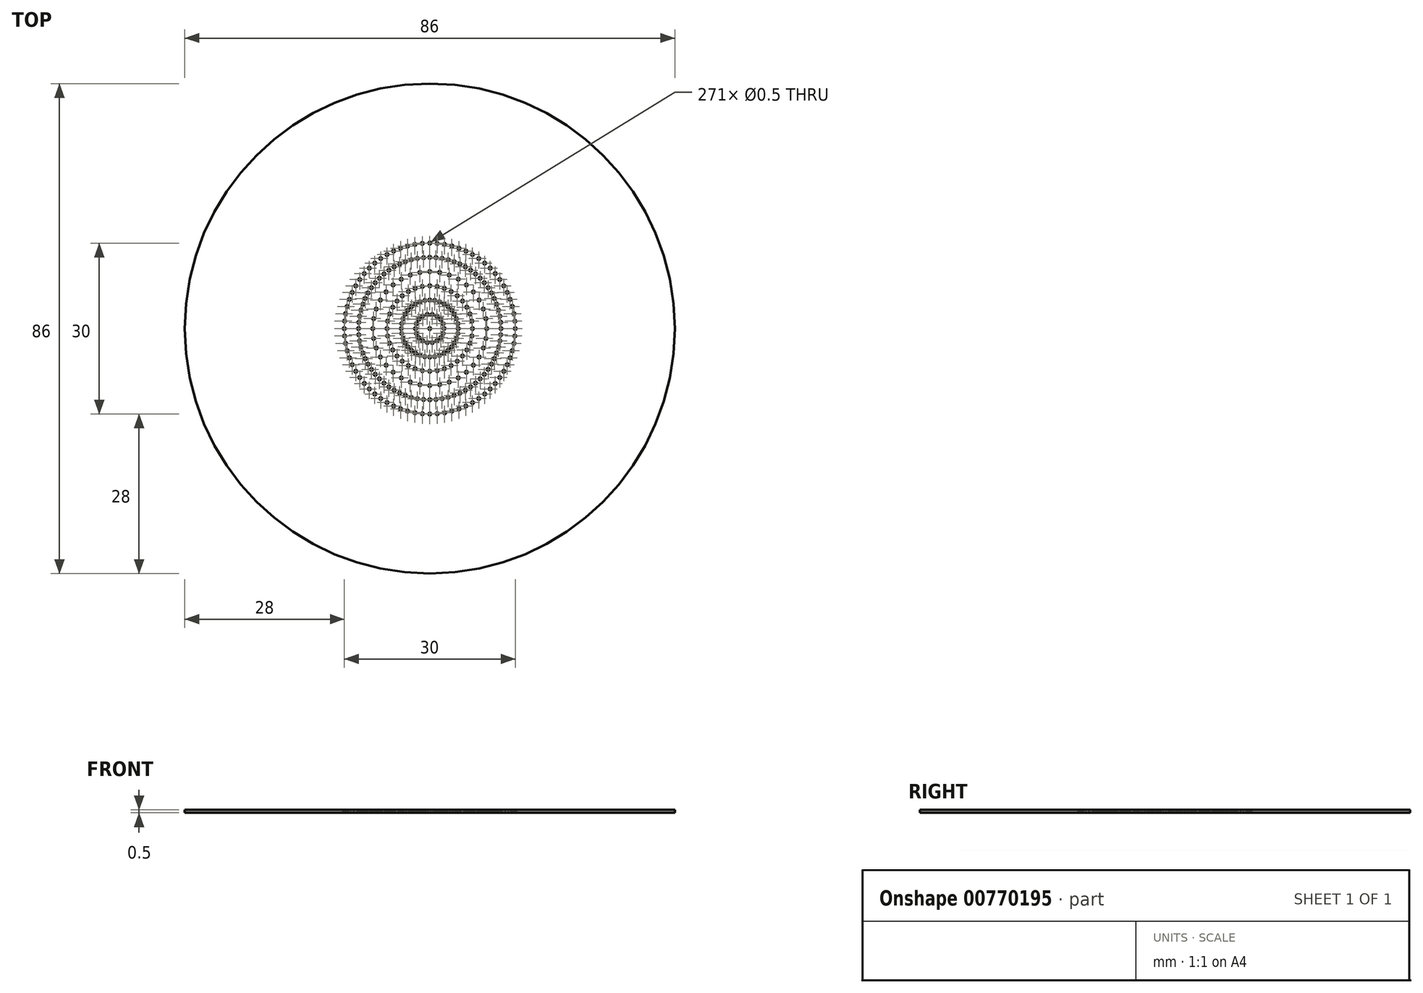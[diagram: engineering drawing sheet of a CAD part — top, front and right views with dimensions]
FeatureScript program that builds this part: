
annotation { "Feature Type Name" : "Feature", "Feature Type Description" : "" }
export const myFeature = defineFeature(function(context is Context, id is Id, definition is map)
    precondition{}
    {
        {
            var Q0;
            Q0=qCreatedBy(makeId("Top.planeOp"),FACE);
            var sketch = newSketch(context, id + "F0", { "sketchPlane" : qUnion([Q0])});
            skCircle(sketch, "E0", {"center": v(0, 0) * mm, "radius": 43 * mm});
            skCircle(sketch, "E1", {"center": v(0, 0) * mm, "radius": 16.13 * mm, "construction": true});
            skSolve(sketch);
        }
        {
            var Q0;
            Q0=makeQuery(id+"F0.imprint","IMPRINT",FACE,{"disambiguationData":[TD([[makeQuery(id+"F0.imprint","IMPRINT",EDGE,{"derivedFrom":sQuery(id+"F0.wireOp",EDGE,"E0")}),1.0]])]});
            extrude(context, id + "F1", {"entities" : qUnion([Q0]), "oppositeDirection" : true, "depth" : 0.5 * mm, "offsetDistance" : 25 * mm});
        }
        {
            var Q0;
            Q0=makeQuery(id+"F0.imprint","IMPRINT",FACE,{"disambiguationData":[TD([[makeQuery(id+"F0.imprint","IMPRINT",EDGE,{"derivedFrom":sQuery(id+"F0.wireOp",EDGE,"E0")}),1.0]])]});
            var sketch = newSketch(context, id + "F2", { "sketchPlane" : qUnion([Q0])});
            skCircle(sketch, "E2", {"center": v(0, 0) * mm, "radius": 0.25 * mm});
            skSolve(sketch);
        }
        {
            var Q0;
            Q0=makeQuery(id+"F0.imprint","IMPRINT",FACE,{"disambiguationData":[TD([[makeQuery(id+"F0.imprint","IMPRINT",EDGE,{"derivedFrom":sQuery(id+"F0.wireOp",EDGE,"E0")}),1.0]])]});
            var sketch = newSketch(context, id + "F3", { "sketchPlane" : qUnion([Q0])});
            skCircle(sketch, "E3.0", {"center": v(0, 0) * mm, "radius": 0.25 * mm});
            skCircle(sketch, "E4.1.0.0", {"center": v(2.5, 0) * mm, "radius": 0.25 * mm});
            skCircle(sketch, "E4.2.0.0", {"center": v(5, 0) * mm, "radius": 0.25 * mm});
            skCircle(sketch, "E4.3.0.0", {"center": v(7.5, 0) * mm, "radius": 0.25 * mm});
            skCircle(sketch, "E4.4.0.0", {"center": v(10, 0) * mm, "radius": 0.25 * mm});
            skCircle(sketch, "E4.5.0.0", {"center": v(12.5, 0) * mm, "radius": 0.25 * mm});
            skCircle(sketch, "E4.6.0.0", {"center": v(15, 0) * mm, "radius": 0.25 * mm});
            skLineSegment(sketch, "E4.direction1", {"start": v(0, 0) * mm, "end": v(2.5, 0) * mm, "construction": true});
            skSolve(sketch);
        }
        {
            var Q0;
            Q0=makeQuery(id+"F0.imprint","IMPRINT",FACE,{"disambiguationData":[TD([[makeQuery(id+"F0.imprint","IMPRINT",EDGE,{"derivedFrom":sQuery(id+"F0.wireOp",EDGE,"E0")}),1.0]])]});
            var sketch = newSketch(context, id + "F4", { "sketchPlane" : qUnion([Q0])});
            skCircle(sketch, "E5.0", {"center": v(2.5, 0) * mm, "radius": 0.25 * mm});
            skCircle(sketch, "E6.1.0", {"center": v(2.35, -0.86) * mm, "radius": 0.25 * mm});
            skCircle(sketch, "E6.2.0", {"center": v(1.92, -1.6) * mm, "radius": 0.25 * mm});
            skCircle(sketch, "E6.3.0", {"center": v(1.25, -2.17) * mm, "radius": 0.25 * mm});
            skCircle(sketch, "E6.4.0", {"center": v(0.43, -2.46) * mm, "radius": 0.25 * mm});
            skCircle(sketch, "E6.5.0", {"center": v(-0.43, -2.46) * mm, "radius": 0.25 * mm});
            skCircle(sketch, "E6.6.0", {"center": v(-1.25, -2.17) * mm, "radius": 0.25 * mm});
            skCircle(sketch, "E6.7.0", {"center": v(-1.92, -1.6) * mm, "radius": 0.25 * mm});
            skCircle(sketch, "E6.8.0", {"center": v(-2.35, -0.86) * mm, "radius": 0.25 * mm});
            skCircle(sketch, "E6.9.0", {"center": v(-2.5, 0) * mm, "radius": 0.25 * mm});
            skCircle(sketch, "E6.10.0", {"center": v(-2.35, 0.86) * mm, "radius": 0.25 * mm});
            skCircle(sketch, "E6.11.0", {"center": v(-1.92, 1.6) * mm, "radius": 0.25 * mm});
            skCircle(sketch, "E6.12.0", {"center": v(-1.25, 2.17) * mm, "radius": 0.25 * mm});
            skCircle(sketch, "E6.13.0", {"center": v(-0.43, 2.46) * mm, "radius": 0.25 * mm});
            skCircle(sketch, "E6.14.0", {"center": v(0.43, 2.46) * mm, "radius": 0.25 * mm});
            skCircle(sketch, "E6.15.0", {"center": v(1.25, 2.17) * mm, "radius": 0.25 * mm});
            skCircle(sketch, "E6.16.0", {"center": v(1.92, 1.6) * mm, "radius": 0.25 * mm});
            skCircle(sketch, "E6.17.0", {"center": v(2.35, 0.86) * mm, "radius": 0.25 * mm});
            skPoint(sketch, "E6.center", {"position": v(0, 0) * mm});
            skLineSegment(sketch, "E6.anchor1", {"start": v(0, 0) * mm, "end": v(2.5, 0) * mm, "construction": true});
            skLineSegment(sketch, "E6.anchor2", {"start": v(0, 0) * mm, "end": v(2.35, 0.86) * mm, "construction": true});
            skSolve(sketch);
        }
        {
            var Q0;
            Q0=makeQuery(id+"F0.imprint","IMPRINT",FACE,{"disambiguationData":[TD([[makeQuery(id+"F0.imprint","IMPRINT",EDGE,{"derivedFrom":sQuery(id+"F0.wireOp",EDGE,"E0")}),1.0]])]});
            var sketch = newSketch(context, id + "F5", { "sketchPlane" : qUnion([Q0])});
            skCircle(sketch, "E7.0", {"center": v(5, 0) * mm, "radius": 0.25 * mm});
            skCircle(sketch, "E7.1", {"center": v(7.5, 0) * mm, "radius": 0.25 * mm});
            skCircle(sketch, "E7.2", {"center": v(10, 0) * mm, "radius": 0.25 * mm});
            skCircle(sketch, "E8.1.0", {"center": v(4.92, 0.87) * mm, "radius": 0.25 * mm});
            skCircle(sketch, "E8.1.1", {"center": v(7.39, 1.3) * mm, "radius": 0.25 * mm});
            skCircle(sketch, "E8.1.2", {"center": v(9.85, 1.74) * mm, "radius": 0.25 * mm});
            skCircle(sketch, "E8.2.0", {"center": v(4.7, 1.71) * mm, "radius": 0.25 * mm});
            skCircle(sketch, "E8.2.1", {"center": v(7.05, 2.57) * mm, "radius": 0.25 * mm});
            skCircle(sketch, "E8.2.2", {"center": v(9.4, 3.42) * mm, "radius": 0.25 * mm});
            skCircle(sketch, "E8.3.0", {"center": v(4.33, 2.5) * mm, "radius": 0.25 * mm});
            skCircle(sketch, "E8.3.1", {"center": v(6.5, 3.75) * mm, "radius": 0.25 * mm});
            skCircle(sketch, "E8.3.2", {"center": v(8.66, 5) * mm, "radius": 0.25 * mm});
            skCircle(sketch, "E8.4.0", {"center": v(3.83, 3.21) * mm, "radius": 0.25 * mm});
            skCircle(sketch, "E8.4.1", {"center": v(5.75, 4.82) * mm, "radius": 0.25 * mm});
            skCircle(sketch, "E8.4.2", {"center": v(7.66, 6.43) * mm, "radius": 0.25 * mm});
            skCircle(sketch, "E8.5.0", {"center": v(3.21, 3.83) * mm, "radius": 0.25 * mm});
            skCircle(sketch, "E8.5.1", {"center": v(4.82, 5.75) * mm, "radius": 0.25 * mm});
            skCircle(sketch, "E8.5.2", {"center": v(6.43, 7.66) * mm, "radius": 0.25 * mm});
            skCircle(sketch, "E8.6.0", {"center": v(2.5, 4.33) * mm, "radius": 0.25 * mm});
            skCircle(sketch, "E8.6.1", {"center": v(3.75, 6.5) * mm, "radius": 0.25 * mm});
            skCircle(sketch, "E8.6.2", {"center": v(5, 8.66) * mm, "radius": 0.25 * mm});
            skCircle(sketch, "E8.7.0", {"center": v(1.71, 4.7) * mm, "radius": 0.25 * mm});
            skCircle(sketch, "E8.7.1", {"center": v(2.57, 7.05) * mm, "radius": 0.25 * mm});
            skCircle(sketch, "E8.7.2", {"center": v(3.42, 9.4) * mm, "radius": 0.25 * mm});
            skCircle(sketch, "E8.8.0", {"center": v(0.87, 4.92) * mm, "radius": 0.25 * mm});
            skCircle(sketch, "E8.8.1", {"center": v(1.3, 7.39) * mm, "radius": 0.25 * mm});
            skCircle(sketch, "E8.8.2", {"center": v(1.74, 9.85) * mm, "radius": 0.25 * mm});
            skCircle(sketch, "E8.9.0", {"center": v(0, 5) * mm, "radius": 0.25 * mm});
            skCircle(sketch, "E8.9.1", {"center": v(0, 7.5) * mm, "radius": 0.25 * mm});
            skCircle(sketch, "E8.9.2", {"center": v(0, 10) * mm, "radius": 0.25 * mm});
            skCircle(sketch, "E8.10.0", {"center": v(-0.87, 4.92) * mm, "radius": 0.25 * mm});
            skCircle(sketch, "E8.10.1", {"center": v(-1.3, 7.39) * mm, "radius": 0.25 * mm});
            skCircle(sketch, "E8.10.2", {"center": v(-1.74, 9.85) * mm, "radius": 0.25 * mm});
            skCircle(sketch, "E8.11.0", {"center": v(-1.71, 4.7) * mm, "radius": 0.25 * mm});
            skCircle(sketch, "E8.11.1", {"center": v(-2.57, 7.05) * mm, "radius": 0.25 * mm});
            skCircle(sketch, "E8.11.2", {"center": v(-3.42, 9.4) * mm, "radius": 0.25 * mm});
            skCircle(sketch, "E8.12.0", {"center": v(-2.5, 4.33) * mm, "radius": 0.25 * mm});
            skCircle(sketch, "E8.12.1", {"center": v(-3.75, 6.5) * mm, "radius": 0.25 * mm});
            skCircle(sketch, "E8.12.2", {"center": v(-5, 8.66) * mm, "radius": 0.25 * mm});
            skCircle(sketch, "E8.13.0", {"center": v(-3.21, 3.83) * mm, "radius": 0.25 * mm});
            skCircle(sketch, "E8.13.1", {"center": v(-4.82, 5.75) * mm, "radius": 0.25 * mm});
            skCircle(sketch, "E8.13.2", {"center": v(-6.43, 7.66) * mm, "radius": 0.25 * mm});
            skCircle(sketch, "E8.14.0", {"center": v(-3.83, 3.21) * mm, "radius": 0.25 * mm});
            skCircle(sketch, "E8.14.1", {"center": v(-5.75, 4.82) * mm, "radius": 0.25 * mm});
            skCircle(sketch, "E8.14.2", {"center": v(-7.66, 6.43) * mm, "radius": 0.25 * mm});
            skCircle(sketch, "E8.15.0", {"center": v(-4.33, 2.5) * mm, "radius": 0.25 * mm});
            skCircle(sketch, "E8.15.1", {"center": v(-6.5, 3.75) * mm, "radius": 0.25 * mm});
            skCircle(sketch, "E8.15.2", {"center": v(-8.66, 5) * mm, "radius": 0.25 * mm});
            skCircle(sketch, "E8.16.0", {"center": v(-4.7, 1.71) * mm, "radius": 0.25 * mm});
            skCircle(sketch, "E8.16.1", {"center": v(-7.05, 2.57) * mm, "radius": 0.25 * mm});
            skCircle(sketch, "E8.16.2", {"center": v(-9.4, 3.42) * mm, "radius": 0.25 * mm});
            skCircle(sketch, "E8.17.0", {"center": v(-4.92, 0.87) * mm, "radius": 0.25 * mm});
            skCircle(sketch, "E8.17.1", {"center": v(-7.39, 1.3) * mm, "radius": 0.25 * mm});
            skCircle(sketch, "E8.17.2", {"center": v(-9.85, 1.74) * mm, "radius": 0.25 * mm});
            skCircle(sketch, "E8.18.0", {"center": v(-5, 0) * mm, "radius": 0.25 * mm});
            skCircle(sketch, "E8.18.1", {"center": v(-7.5, 0) * mm, "radius": 0.25 * mm});
            skCircle(sketch, "E8.18.2", {"center": v(-10, 0) * mm, "radius": 0.25 * mm});
            skCircle(sketch, "E8.19.0", {"center": v(-4.92, -0.87) * mm, "radius": 0.25 * mm});
            skCircle(sketch, "E8.19.1", {"center": v(-7.39, -1.3) * mm, "radius": 0.25 * mm});
            skCircle(sketch, "E8.19.2", {"center": v(-9.85, -1.74) * mm, "radius": 0.25 * mm});
            skCircle(sketch, "E8.20.0", {"center": v(-4.7, -1.71) * mm, "radius": 0.25 * mm});
            skCircle(sketch, "E8.20.1", {"center": v(-7.05, -2.57) * mm, "radius": 0.25 * mm});
            skCircle(sketch, "E8.20.2", {"center": v(-9.4, -3.42) * mm, "radius": 0.25 * mm});
            skCircle(sketch, "E8.21.0", {"center": v(-4.33, -2.5) * mm, "radius": 0.25 * mm});
            skCircle(sketch, "E8.21.1", {"center": v(-6.5, -3.75) * mm, "radius": 0.25 * mm});
            skCircle(sketch, "E8.21.2", {"center": v(-8.66, -5) * mm, "radius": 0.25 * mm});
            skCircle(sketch, "E8.22.0", {"center": v(-3.83, -3.21) * mm, "radius": 0.25 * mm});
            skCircle(sketch, "E8.22.1", {"center": v(-5.75, -4.82) * mm, "radius": 0.25 * mm});
            skCircle(sketch, "E8.22.2", {"center": v(-7.66, -6.43) * mm, "radius": 0.25 * mm});
            skCircle(sketch, "E8.23.0", {"center": v(-3.21, -3.83) * mm, "radius": 0.25 * mm});
            skCircle(sketch, "E8.23.1", {"center": v(-4.82, -5.75) * mm, "radius": 0.25 * mm});
            skCircle(sketch, "E8.23.2", {"center": v(-6.43, -7.66) * mm, "radius": 0.25 * mm});
            skCircle(sketch, "E8.24.0", {"center": v(-2.5, -4.33) * mm, "radius": 0.25 * mm});
            skCircle(sketch, "E8.24.1", {"center": v(-3.75, -6.5) * mm, "radius": 0.25 * mm});
            skCircle(sketch, "E8.24.2", {"center": v(-5, -8.66) * mm, "radius": 0.25 * mm});
            skCircle(sketch, "E8.25.0", {"center": v(-1.71, -4.7) * mm, "radius": 0.25 * mm});
            skCircle(sketch, "E8.25.1", {"center": v(-2.57, -7.05) * mm, "radius": 0.25 * mm});
            skCircle(sketch, "E8.25.2", {"center": v(-3.42, -9.4) * mm, "radius": 0.25 * mm});
            skCircle(sketch, "E8.26.0", {"center": v(-0.87, -4.92) * mm, "radius": 0.25 * mm});
            skCircle(sketch, "E8.26.1", {"center": v(-1.3, -7.39) * mm, "radius": 0.25 * mm});
            skCircle(sketch, "E8.26.2", {"center": v(-1.74, -9.85) * mm, "radius": 0.25 * mm});
            skCircle(sketch, "E8.27.0", {"center": v(0, -5) * mm, "radius": 0.25 * mm});
            skCircle(sketch, "E8.27.1", {"center": v(0, -7.5) * mm, "radius": 0.25 * mm});
            skCircle(sketch, "E8.27.2", {"center": v(0, -10) * mm, "radius": 0.25 * mm});
            skCircle(sketch, "E8.28.0", {"center": v(0.87, -4.92) * mm, "radius": 0.25 * mm});
            skCircle(sketch, "E8.28.1", {"center": v(1.3, -7.39) * mm, "radius": 0.25 * mm});
            skCircle(sketch, "E8.28.2", {"center": v(1.74, -9.85) * mm, "radius": 0.25 * mm});
            skCircle(sketch, "E8.29.0", {"center": v(1.71, -4.7) * mm, "radius": 0.25 * mm});
            skCircle(sketch, "E8.29.1", {"center": v(2.57, -7.05) * mm, "radius": 0.25 * mm});
            skCircle(sketch, "E8.29.2", {"center": v(3.42, -9.4) * mm, "radius": 0.25 * mm});
            skCircle(sketch, "E8.30.0", {"center": v(2.5, -4.33) * mm, "radius": 0.25 * mm});
            skCircle(sketch, "E8.30.1", {"center": v(3.75, -6.5) * mm, "radius": 0.25 * mm});
            skCircle(sketch, "E8.30.2", {"center": v(5, -8.66) * mm, "radius": 0.25 * mm});
            skCircle(sketch, "E8.31.0", {"center": v(3.21, -3.83) * mm, "radius": 0.25 * mm});
            skCircle(sketch, "E8.31.1", {"center": v(4.82, -5.75) * mm, "radius": 0.25 * mm});
            skCircle(sketch, "E8.31.2", {"center": v(6.43, -7.66) * mm, "radius": 0.25 * mm});
            skCircle(sketch, "E8.32.0", {"center": v(3.83, -3.21) * mm, "radius": 0.25 * mm});
            skCircle(sketch, "E8.32.1", {"center": v(5.75, -4.82) * mm, "radius": 0.25 * mm});
            skCircle(sketch, "E8.32.2", {"center": v(7.66, -6.43) * mm, "radius": 0.25 * mm});
            skCircle(sketch, "E8.33.0", {"center": v(4.33, -2.5) * mm, "radius": 0.25 * mm});
            skCircle(sketch, "E8.33.1", {"center": v(6.5, -3.75) * mm, "radius": 0.25 * mm});
            skCircle(sketch, "E8.33.2", {"center": v(8.66, -5) * mm, "radius": 0.25 * mm});
            skCircle(sketch, "E8.34.0", {"center": v(4.7, -1.71) * mm, "radius": 0.25 * mm});
            skCircle(sketch, "E8.34.1", {"center": v(7.05, -2.57) * mm, "radius": 0.25 * mm});
            skCircle(sketch, "E8.34.2", {"center": v(9.4, -3.42) * mm, "radius": 0.25 * mm});
            skCircle(sketch, "E8.35.0", {"center": v(4.92, -0.87) * mm, "radius": 0.25 * mm});
            skCircle(sketch, "E8.35.1", {"center": v(7.39, -1.3) * mm, "radius": 0.25 * mm});
            skCircle(sketch, "E8.35.2", {"center": v(9.85, -1.74) * mm, "radius": 0.25 * mm});
            skPoint(sketch, "E8.center", {"position": v(0, 0) * mm});
            skSolve(sketch);
        }
        {
            var Q0;
            Q0=makeQuery(id+"F0.imprint","IMPRINT",FACE,{"disambiguationData":[TD([[makeQuery(id+"F0.imprint","IMPRINT",EDGE,{"derivedFrom":sQuery(id+"F0.wireOp",EDGE,"E0")}),1.0]])]});
            var sketch = newSketch(context, id + "F6", { "sketchPlane" : qUnion([Q0])});
            skCircle(sketch, "E9.0", {"center": v(12.5, 0) * mm, "radius": 0.25 * mm});
            skCircle(sketch, "E9.1", {"center": v(15, 0) * mm, "radius": 0.25 * mm});
            skCircle(sketch, "E10.1.0", {"center": v(12.45, 1.09) * mm, "radius": 0.25 * mm});
            skCircle(sketch, "E10.1.1", {"center": v(14.94, 1.3) * mm, "radius": 0.25 * mm});
            skCircle(sketch, "E10.2.0", {"center": v(12.31, 2.17) * mm, "radius": 0.25 * mm});
            skCircle(sketch, "E10.2.1", {"center": v(14.77, 2.6) * mm, "radius": 0.25 * mm});
            skCircle(sketch, "E10.3.0", {"center": v(12.07, 3.24) * mm, "radius": 0.25 * mm});
            skCircle(sketch, "E10.3.1", {"center": v(14.49, 3.88) * mm, "radius": 0.25 * mm});
            skCircle(sketch, "E10.4.0", {"center": v(11.75, 4.28) * mm, "radius": 0.25 * mm});
            skCircle(sketch, "E10.4.1", {"center": v(14.1, 5.13) * mm, "radius": 0.25 * mm});
            skCircle(sketch, "E10.5.0", {"center": v(11.33, 5.28) * mm, "radius": 0.25 * mm});
            skCircle(sketch, "E10.5.1", {"center": v(13.6, 6.34) * mm, "radius": 0.25 * mm});
            skCircle(sketch, "E10.6.0", {"center": v(10.83, 6.25) * mm, "radius": 0.25 * mm});
            skCircle(sketch, "E10.6.1", {"center": v(13, 7.5) * mm, "radius": 0.25 * mm});
            skCircle(sketch, "E10.7.0", {"center": v(10.24, 7.17) * mm, "radius": 0.25 * mm});
            skCircle(sketch, "E10.7.1", {"center": v(12.29, 8.6) * mm, "radius": 0.25 * mm});
            skCircle(sketch, "E10.8.0", {"center": v(9.58, 8.03) * mm, "radius": 0.25 * mm});
            skCircle(sketch, "E10.8.1", {"center": v(11.5, 9.64) * mm, "radius": 0.25 * mm});
            skCircle(sketch, "E10.9.0", {"center": v(8.84, 8.84) * mm, "radius": 0.25 * mm});
            skCircle(sketch, "E10.9.1", {"center": v(10.6, 10.6) * mm, "radius": 0.25 * mm});
            skCircle(sketch, "E10.10.0", {"center": v(8.03, 9.58) * mm, "radius": 0.25 * mm});
            skCircle(sketch, "E10.10.1", {"center": v(9.64, 11.5) * mm, "radius": 0.25 * mm});
            skCircle(sketch, "E10.11.0", {"center": v(7.17, 10.24) * mm, "radius": 0.25 * mm});
            skCircle(sketch, "E10.11.1", {"center": v(8.6, 12.29) * mm, "radius": 0.25 * mm});
            skCircle(sketch, "E10.12.0", {"center": v(6.25, 10.83) * mm, "radius": 0.25 * mm});
            skCircle(sketch, "E10.12.1", {"center": v(7.5, 13) * mm, "radius": 0.25 * mm});
            skCircle(sketch, "E10.13.0", {"center": v(5.28, 11.33) * mm, "radius": 0.25 * mm});
            skCircle(sketch, "E10.13.1", {"center": v(6.34, 13.6) * mm, "radius": 0.25 * mm});
            skCircle(sketch, "E10.14.0", {"center": v(4.28, 11.75) * mm, "radius": 0.25 * mm});
            skCircle(sketch, "E10.14.1", {"center": v(5.13, 14.1) * mm, "radius": 0.25 * mm});
            skCircle(sketch, "E10.15.0", {"center": v(3.24, 12.07) * mm, "radius": 0.25 * mm});
            skCircle(sketch, "E10.15.1", {"center": v(3.88, 14.49) * mm, "radius": 0.25 * mm});
            skCircle(sketch, "E10.16.0", {"center": v(2.17, 12.31) * mm, "radius": 0.25 * mm});
            skCircle(sketch, "E10.16.1", {"center": v(2.6, 14.77) * mm, "radius": 0.25 * mm});
            skCircle(sketch, "E10.17.0", {"center": v(1.09, 12.45) * mm, "radius": 0.25 * mm});
            skCircle(sketch, "E10.17.1", {"center": v(1.3, 14.94) * mm, "radius": 0.25 * mm});
            skCircle(sketch, "E10.18.0", {"center": v(0, 12.5) * mm, "radius": 0.25 * mm});
            skCircle(sketch, "E10.18.1", {"center": v(0, 15) * mm, "radius": 0.25 * mm});
            skCircle(sketch, "E10.19.0", {"center": v(-1.09, 12.45) * mm, "radius": 0.25 * mm});
            skCircle(sketch, "E10.19.1", {"center": v(-1.3, 14.94) * mm, "radius": 0.25 * mm});
            skCircle(sketch, "E10.20.0", {"center": v(-2.17, 12.31) * mm, "radius": 0.25 * mm});
            skCircle(sketch, "E10.20.1", {"center": v(-2.6, 14.77) * mm, "radius": 0.25 * mm});
            skCircle(sketch, "E10.21.0", {"center": v(-3.24, 12.07) * mm, "radius": 0.25 * mm});
            skCircle(sketch, "E10.21.1", {"center": v(-3.88, 14.49) * mm, "radius": 0.25 * mm});
            skCircle(sketch, "E10.22.0", {"center": v(-4.28, 11.75) * mm, "radius": 0.25 * mm});
            skCircle(sketch, "E10.22.1", {"center": v(-5.13, 14.1) * mm, "radius": 0.25 * mm});
            skCircle(sketch, "E10.23.0", {"center": v(-5.28, 11.33) * mm, "radius": 0.25 * mm});
            skCircle(sketch, "E10.23.1", {"center": v(-6.34, 13.6) * mm, "radius": 0.25 * mm});
            skCircle(sketch, "E10.24.0", {"center": v(-6.25, 10.83) * mm, "radius": 0.25 * mm});
            skCircle(sketch, "E10.24.1", {"center": v(-7.5, 13) * mm, "radius": 0.25 * mm});
            skCircle(sketch, "E10.25.0", {"center": v(-7.17, 10.24) * mm, "radius": 0.25 * mm});
            skCircle(sketch, "E10.25.1", {"center": v(-8.6, 12.29) * mm, "radius": 0.25 * mm});
            skCircle(sketch, "E10.26.0", {"center": v(-8.03, 9.58) * mm, "radius": 0.25 * mm});
            skCircle(sketch, "E10.26.1", {"center": v(-9.64, 11.5) * mm, "radius": 0.25 * mm});
            skCircle(sketch, "E10.27.0", {"center": v(-8.84, 8.84) * mm, "radius": 0.25 * mm});
            skCircle(sketch, "E10.27.1", {"center": v(-10.6, 10.6) * mm, "radius": 0.25 * mm});
            skCircle(sketch, "E10.28.0", {"center": v(-9.58, 8.03) * mm, "radius": 0.25 * mm});
            skCircle(sketch, "E10.28.1", {"center": v(-11.5, 9.64) * mm, "radius": 0.25 * mm});
            skCircle(sketch, "E10.29.0", {"center": v(-10.24, 7.17) * mm, "radius": 0.25 * mm});
            skCircle(sketch, "E10.29.1", {"center": v(-12.29, 8.6) * mm, "radius": 0.25 * mm});
            skCircle(sketch, "E10.30.0", {"center": v(-10.83, 6.25) * mm, "radius": 0.25 * mm});
            skCircle(sketch, "E10.30.1", {"center": v(-13, 7.5) * mm, "radius": 0.25 * mm});
            skCircle(sketch, "E10.31.0", {"center": v(-11.33, 5.28) * mm, "radius": 0.25 * mm});
            skCircle(sketch, "E10.31.1", {"center": v(-13.6, 6.34) * mm, "radius": 0.25 * mm});
            skCircle(sketch, "E10.32.0", {"center": v(-11.75, 4.28) * mm, "radius": 0.25 * mm});
            skCircle(sketch, "E10.32.1", {"center": v(-14.1, 5.13) * mm, "radius": 0.25 * mm});
            skCircle(sketch, "E10.33.0", {"center": v(-12.07, 3.24) * mm, "radius": 0.25 * mm});
            skCircle(sketch, "E10.33.1", {"center": v(-14.49, 3.88) * mm, "radius": 0.25 * mm});
            skCircle(sketch, "E10.34.0", {"center": v(-12.31, 2.17) * mm, "radius": 0.25 * mm});
            skCircle(sketch, "E10.34.1", {"center": v(-14.77, 2.6) * mm, "radius": 0.25 * mm});
            skCircle(sketch, "E10.35.0", {"center": v(-12.45, 1.09) * mm, "radius": 0.25 * mm});
            skCircle(sketch, "E10.35.1", {"center": v(-14.94, 1.3) * mm, "radius": 0.25 * mm});
            skCircle(sketch, "E10.36.0", {"center": v(-12.5, 0) * mm, "radius": 0.25 * mm});
            skCircle(sketch, "E10.36.1", {"center": v(-15, 0) * mm, "radius": 0.25 * mm});
            skCircle(sketch, "E10.37.0", {"center": v(-12.45, -1.09) * mm, "radius": 0.25 * mm});
            skCircle(sketch, "E10.37.1", {"center": v(-14.94, -1.3) * mm, "radius": 0.25 * mm});
            skCircle(sketch, "E10.38.0", {"center": v(-12.31, -2.17) * mm, "radius": 0.25 * mm});
            skCircle(sketch, "E10.38.1", {"center": v(-14.77, -2.6) * mm, "radius": 0.25 * mm});
            skCircle(sketch, "E10.39.0", {"center": v(-12.07, -3.24) * mm, "radius": 0.25 * mm});
            skCircle(sketch, "E10.39.1", {"center": v(-14.49, -3.88) * mm, "radius": 0.25 * mm});
            skCircle(sketch, "E10.40.0", {"center": v(-11.75, -4.28) * mm, "radius": 0.25 * mm});
            skCircle(sketch, "E10.40.1", {"center": v(-14.1, -5.13) * mm, "radius": 0.25 * mm});
            skCircle(sketch, "E10.41.0", {"center": v(-11.33, -5.28) * mm, "radius": 0.25 * mm});
            skCircle(sketch, "E10.41.1", {"center": v(-13.6, -6.34) * mm, "radius": 0.25 * mm});
            skCircle(sketch, "E10.42.0", {"center": v(-10.83, -6.25) * mm, "radius": 0.25 * mm});
            skCircle(sketch, "E10.42.1", {"center": v(-13, -7.5) * mm, "radius": 0.25 * mm});
            skCircle(sketch, "E10.43.0", {"center": v(-10.24, -7.17) * mm, "radius": 0.25 * mm});
            skCircle(sketch, "E10.43.1", {"center": v(-12.29, -8.6) * mm, "radius": 0.25 * mm});
            skCircle(sketch, "E10.44.0", {"center": v(-9.58, -8.03) * mm, "radius": 0.25 * mm});
            skCircle(sketch, "E10.44.1", {"center": v(-11.5, -9.64) * mm, "radius": 0.25 * mm});
            skCircle(sketch, "E10.45.0", {"center": v(-8.84, -8.84) * mm, "radius": 0.25 * mm});
            skCircle(sketch, "E10.45.1", {"center": v(-10.6, -10.6) * mm, "radius": 0.25 * mm});
            skCircle(sketch, "E10.46.0", {"center": v(-8.03, -9.58) * mm, "radius": 0.25 * mm});
            skCircle(sketch, "E10.46.1", {"center": v(-9.64, -11.5) * mm, "radius": 0.25 * mm});
            skCircle(sketch, "E10.47.0", {"center": v(-7.17, -10.24) * mm, "radius": 0.25 * mm});
            skCircle(sketch, "E10.47.1", {"center": v(-8.6, -12.29) * mm, "radius": 0.25 * mm});
            skCircle(sketch, "E10.48.0", {"center": v(-6.25, -10.83) * mm, "radius": 0.25 * mm});
            skCircle(sketch, "E10.48.1", {"center": v(-7.5, -13) * mm, "radius": 0.25 * mm});
            skCircle(sketch, "E10.49.0", {"center": v(-5.28, -11.33) * mm, "radius": 0.25 * mm});
            skCircle(sketch, "E10.49.1", {"center": v(-6.34, -13.6) * mm, "radius": 0.25 * mm});
            skCircle(sketch, "E10.50.0", {"center": v(-4.28, -11.75) * mm, "radius": 0.25 * mm});
            skCircle(sketch, "E10.50.1", {"center": v(-5.13, -14.1) * mm, "radius": 0.25 * mm});
            skCircle(sketch, "E10.51.0", {"center": v(-3.24, -12.07) * mm, "radius": 0.25 * mm});
            skCircle(sketch, "E10.51.1", {"center": v(-3.88, -14.49) * mm, "radius": 0.25 * mm});
            skCircle(sketch, "E10.52.0", {"center": v(-2.17, -12.31) * mm, "radius": 0.25 * mm});
            skCircle(sketch, "E10.52.1", {"center": v(-2.6, -14.77) * mm, "radius": 0.25 * mm});
            skCircle(sketch, "E10.53.0", {"center": v(-1.09, -12.45) * mm, "radius": 0.25 * mm});
            skCircle(sketch, "E10.53.1", {"center": v(-1.3, -14.94) * mm, "radius": 0.25 * mm});
            skCircle(sketch, "E10.54.0", {"center": v(0, -12.5) * mm, "radius": 0.25 * mm});
            skCircle(sketch, "E10.54.1", {"center": v(0, -15) * mm, "radius": 0.25 * mm});
            skCircle(sketch, "E10.55.0", {"center": v(1.09, -12.45) * mm, "radius": 0.25 * mm});
            skCircle(sketch, "E10.55.1", {"center": v(1.3, -14.94) * mm, "radius": 0.25 * mm});
            skCircle(sketch, "E10.56.0", {"center": v(2.17, -12.31) * mm, "radius": 0.25 * mm});
            skCircle(sketch, "E10.56.1", {"center": v(2.6, -14.77) * mm, "radius": 0.25 * mm});
            skCircle(sketch, "E10.57.0", {"center": v(3.24, -12.07) * mm, "radius": 0.25 * mm});
            skCircle(sketch, "E10.57.1", {"center": v(3.88, -14.49) * mm, "radius": 0.25 * mm});
            skCircle(sketch, "E10.58.0", {"center": v(4.28, -11.75) * mm, "radius": 0.25 * mm});
            skCircle(sketch, "E10.58.1", {"center": v(5.13, -14.1) * mm, "radius": 0.25 * mm});
            skCircle(sketch, "E10.59.0", {"center": v(5.28, -11.33) * mm, "radius": 0.25 * mm});
            skCircle(sketch, "E10.59.1", {"center": v(6.34, -13.6) * mm, "radius": 0.25 * mm});
            skCircle(sketch, "E10.60.0", {"center": v(6.25, -10.83) * mm, "radius": 0.25 * mm});
            skCircle(sketch, "E10.60.1", {"center": v(7.5, -13) * mm, "radius": 0.25 * mm});
            skCircle(sketch, "E10.61.0", {"center": v(7.17, -10.24) * mm, "radius": 0.25 * mm});
            skCircle(sketch, "E10.61.1", {"center": v(8.6, -12.29) * mm, "radius": 0.25 * mm});
            skCircle(sketch, "E10.62.0", {"center": v(8.03, -9.58) * mm, "radius": 0.25 * mm});
            skCircle(sketch, "E10.62.1", {"center": v(9.64, -11.5) * mm, "radius": 0.25 * mm});
            skCircle(sketch, "E10.63.0", {"center": v(8.84, -8.84) * mm, "radius": 0.25 * mm});
            skCircle(sketch, "E10.63.1", {"center": v(10.6, -10.6) * mm, "radius": 0.25 * mm});
            skCircle(sketch, "E10.64.0", {"center": v(9.58, -8.03) * mm, "radius": 0.25 * mm});
            skCircle(sketch, "E10.64.1", {"center": v(11.5, -9.64) * mm, "radius": 0.25 * mm});
            skCircle(sketch, "E10.65.0", {"center": v(10.24, -7.17) * mm, "radius": 0.25 * mm});
            skCircle(sketch, "E10.65.1", {"center": v(12.29, -8.6) * mm, "radius": 0.25 * mm});
            skCircle(sketch, "E10.66.0", {"center": v(10.83, -6.25) * mm, "radius": 0.25 * mm});
            skCircle(sketch, "E10.66.1", {"center": v(13, -7.5) * mm, "radius": 0.25 * mm});
            skCircle(sketch, "E10.67.0", {"center": v(11.33, -5.28) * mm, "radius": 0.25 * mm});
            skCircle(sketch, "E10.67.1", {"center": v(13.6, -6.34) * mm, "radius": 0.25 * mm});
            skCircle(sketch, "E10.68.0", {"center": v(11.75, -4.28) * mm, "radius": 0.25 * mm});
            skCircle(sketch, "E10.68.1", {"center": v(14.1, -5.13) * mm, "radius": 0.25 * mm});
            skCircle(sketch, "E10.69.0", {"center": v(12.07, -3.24) * mm, "radius": 0.25 * mm});
            skCircle(sketch, "E10.69.1", {"center": v(14.49, -3.88) * mm, "radius": 0.25 * mm});
            skCircle(sketch, "E10.70.0", {"center": v(12.31, -2.17) * mm, "radius": 0.25 * mm});
            skCircle(sketch, "E10.70.1", {"center": v(14.77, -2.6) * mm, "radius": 0.25 * mm});
            skCircle(sketch, "E10.71.0", {"center": v(12.45, -1.09) * mm, "radius": 0.25 * mm});
            skCircle(sketch, "E10.71.1", {"center": v(14.94, -1.3) * mm, "radius": 0.25 * mm});
            skPoint(sketch, "E10.center", {"position": v(0, 0) * mm});
            skSolve(sketch);
        }
        {
            var Q0;
            Q0 = qSketchRegion(id + "F2", true);
            extrude(context, id + "F7", {"entities" : qUnion([Q0]), "operationType" : NewBodyOperationType.REMOVE, "oppositeDirection" : true, "depth" : 25 * mm, "offsetDistance" : 25 * mm});
        }
        {
            var Q0;
            Q0 = qSketchRegion(id + "F3", true);
            var Q1;
            Q1 = qSketchRegion(id + "F4", true);
            var Q2;
            Q2 = qSketchRegion(id + "F5", true);
            var Q3;
            Q3 = qSketchRegion(id + "F6", true);
            extrude(context, id + "F8", {"entities" : qUnion([Q0, Q1, Q2, Q3]), "operationType" : NewBodyOperationType.REMOVE, "oppositeDirection" : true, "depth" : 25 * mm, "offsetDistance" : 25 * mm});
        }
    });
